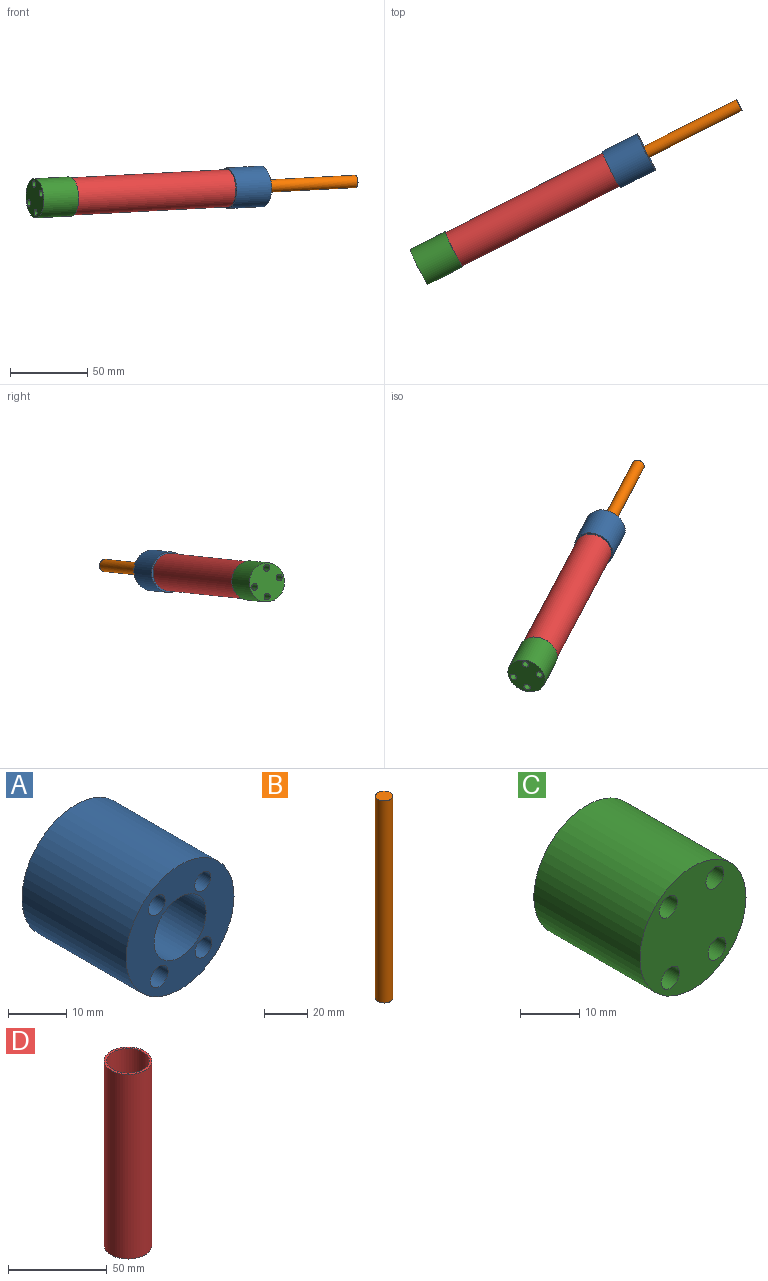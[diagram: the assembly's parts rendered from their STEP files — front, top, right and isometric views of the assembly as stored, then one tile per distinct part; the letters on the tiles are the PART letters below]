
ASSEMBLY  parts=4 mates=3
PART A: 10 faces, bbox 26.3x25.4x26.3 mm
  f0: cylinder r=4mm len=8mm, axis (0,1,0), area 191.5mm2, adj f1,f2
  f1: plane 12.7x12.7mm, normal (0,-1,0), area 76.4mm2, adj f0,f3
  f2: plane 26.3x26.3mm, normal (0,1,0), area 440.7mm2, adj f0,f4,f5,f6,f7,f8
  f3: cylinder r=6.35mm len=17.78mm, axis (0,1,0), area 709.4mm2, adj f1,f9
  f4: cylinder r=1.94mm len=25.4mm, axis (0,1,0), area 310.1mm2, adj f2,f9
  f5: cylinder r=2.02mm len=25.4mm, axis (0,1,0), area 322.3mm2, adj f2,f9
  f6: cylinder r=2.16mm len=25.4mm, axis (0,1,0), area 344.6mm2, adj f2,f9
  f7: cylinder r=2.02mm len=25.4mm, axis (0,1,0), area 322.3mm2, adj f2,f9
  f8: cylinder r=13.15mm len=26.3mm, axis (0,1,0), area 2098.3mm2, adj f2,f9
  f9: plane 26.3x26.3mm, normal (0,-1,0), area 364.3mm2, adj f3,f4,f5,f6,f7,f8
PART B: 3 faces, bbox 8x8x114.3 mm
  f0: cylinder r=3.99mm len=114.3mm, axis (0,0,-1), area 2863.9mm2, adj f1,f2
  f1: plane 7.98x7.98mm, normal (0,0,-1), area 50mm2, adj f0
  f2: plane 7.98x7.98mm, normal (0,0,1), area 50mm2, adj f0
PART C: 7 faces, bbox 25.4x25.4x25.4 mm
  f0: cylinder r=2.16mm len=25.4mm, axis (0,1,0), area 344.6mm2, adj f5,f6
  f1: cylinder r=2.16mm len=25.4mm, axis (0,1,0), area 344.6mm2, adj f5,f6
  f2: cylinder r=2.16mm len=25.4mm, axis (0,1,0), area 344.6mm2, adj f5,f6
  f3: cylinder r=2.16mm len=25.4mm, axis (0,1,0), area 344.6mm2, adj f5,f6
  f4: cylinder r=12.7mm len=25.4mm, axis (0,1,0), area 2026.8mm2, adj f5,f6
  f5: plane 25.4x25.4mm, normal (0,-1,0), area 448.1mm2, adj f0,f1,f2,f3,f4
  f6: plane 25.4x25.4mm, normal (0,1,0), area 448.1mm2, adj f0,f1,f2,f3,f4
PART D: 4 faces, bbox 24.1x24.1x114.3 mm
  f0: cylinder r=10.79mm len=114.3mm, axis (0,0,-1), area 7752.6mm2, adj f2,f3
  f1: cylinder r=12.06mm len=114.3mm, axis (0,0,-1), area 8664.7mm2, adj f2,f3
  f2: plane 24.13x24.13mm, normal (0,0,1), area 91.2mm2, adj f0,f1
  f3: plane 24.13x24.13mm, normal (0,0,-1), area 91.2mm2, adj f0,f1
PLACE A rot(axis=(0.31,0.44,-0.84),71.3deg) t=(163.21,-11.86,81.67)mm
PLACE B rot(axis=(0.07,0.87,0.48),104deg) t=(130.06,-48.66,66.21)mm
PLACE C rot(axis=(0.31,0.44,-0.84),71.3deg) t=(27.57,-48.92,37.21)mm
PLACE D rot(axis=(0.52,-0.85,-0.08),93.1deg) t=(136.26,-15.48,87.1)mm fixed
MATE fastened C.f4 <-> D.f0  axis (0.89,0.45,0.05) through (38.68,-74.84,75.1)mm
MATE slider A.f0 <-> B.f0  axis (0.89,0.45,0.05) through (163.21,-11.86,81.67)mm
MATE fastened A.f0 <-> D.f0  axis (-0.89,-0.45,-0.05) through (140.57,-23.31,80.47)mm
